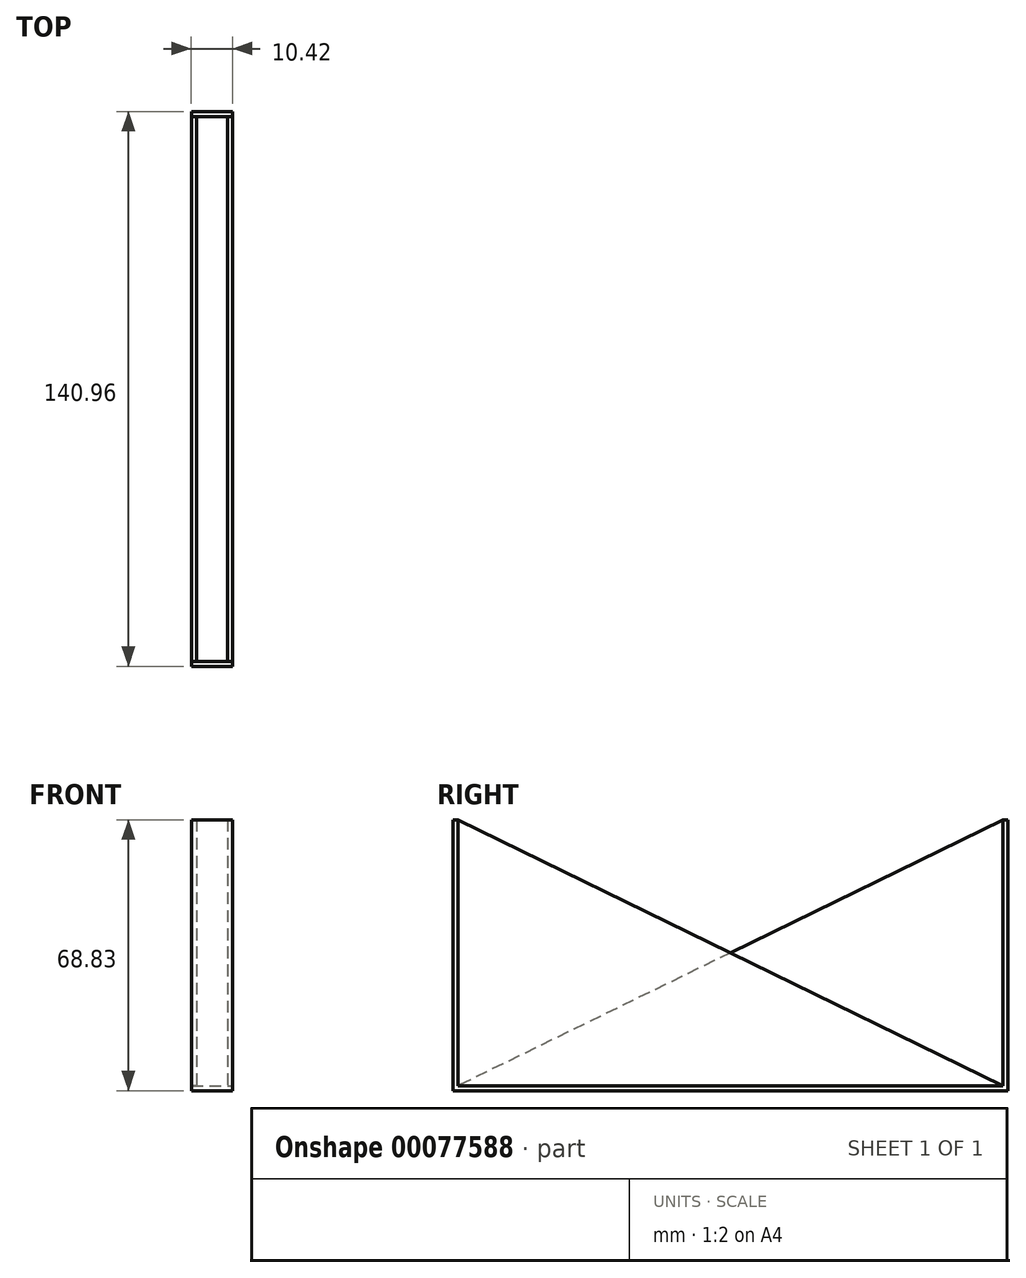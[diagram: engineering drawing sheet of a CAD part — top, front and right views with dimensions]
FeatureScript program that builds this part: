
annotation { "Feature Type Name" : "Feature", "Feature Type Description" : "" }
export const myFeature = defineFeature(function(context is Context, id is Id, definition is map)
    precondition{}
    {
        {
            var Q0;
            Q0=qCreatedBy(makeId("Top.planeOp"),FACE);
            var sketch = newSketch(context, id + "F0", { "sketchPlane" : qUnion([Q0])});
            skLineSegment(sketch, "E0.bottom", {"start": v(5.2, -70.48) * mm, "end": v(-5.2, -70.48) * mm});
            skLineSegment(sketch, "E0.top", {"start": v(5.2, 70.48) * mm, "end": v(-5.2, 70.48) * mm});
            skLineSegment(sketch, "E0.left", {"start": v(5.2, -70.48) * mm, "end": v(5.2, 70.48) * mm});
            skLineSegment(sketch, "E0.right", {"start": v(-5.2, -70.48) * mm, "end": v(-5.2, 70.48) * mm});
            skPoint(sketch, "E0.middle", {"position": v(0, 0) * mm});
            skSolve(sketch);
        }
        {
            var Q0;
            Q0=makeQuery(id+"F0.imprint","IMPRINT",FACE,{"disambiguationData":[TD([[makeQuery(id+"F0.imprint","IMPRINT",EDGE,{"derivedFrom":sQuery(id+"F0.wireOp",EDGE,"E0.bottom")}),-1.0]])]});
            extrude(context, id + "F1", {"entities" : qUnion([Q0]), "depth" : 1.27 * mm});
        }
        {
            var Q0;
            Q0=makeQuery(id+"F1.opExtrude","CAP_FACE",FACE,{"disambiguationData":[OSD([sQuery(id+"F0.wireOp",EDGE,"E0.bottom"),sQuery(id+"F0.wireOp",EDGE,"E0.top"),sQuery(id+"F0.wireOp",EDGE,"E0.left"),sQuery(id+"F0.wireOp",EDGE,"E0.right")])],"isStart":false});
            var sketch = newSketch(context, id + "F2", { "sketchPlane" : qUnion([Q0])});
            skLineSegment(sketch, "E1.bottom", {"start": v(-5.2, -70.48) * mm, "end": v(5.2, -70.48) * mm});
            skLineSegment(sketch, "E1.top", {"start": v(-5.2, -69.22) * mm, "end": v(5.2, -69.22) * mm});
            skLineSegment(sketch, "E1.left", {"start": v(-5.2, -70.48) * mm, "end": v(-5.2, -69.22) * mm});
            skLineSegment(sketch, "E1.right", {"start": v(5.2, -70.48) * mm, "end": v(5.2, -69.22) * mm});
            skLineSegment(sketch, "E2.bottom", {"start": v(-5.2, 70.48) * mm, "end": v(5.2, 70.48) * mm});
            skLineSegment(sketch, "E2.top", {"start": v(-5.2, 69.22) * mm, "end": v(5.2, 69.22) * mm});
            skLineSegment(sketch, "E2.left", {"start": v(-5.2, 70.48) * mm, "end": v(-5.2, 69.22) * mm});
            skLineSegment(sketch, "E2.right", {"start": v(5.2, 70.48) * mm, "end": v(5.2, 69.22) * mm});
            skSolve(sketch);
        }
        {
            var Q0;
            Q0=makeQuery(id+"F2.imprint","IMPRINT",FACE,{"disambiguationData":[TD([[makeQuery(id+"F2.imprint","IMPRINT",EDGE,{"derivedFrom":sQuery(id+"F2.wireOp",EDGE,"E1.bottom")}),-1.0]])]});
            extrude(context, id + "F3", {"entities" : qUnion([Q0]), "operationType" : NewBodyOperationType.ADD, "depth" : 67.56 * mm});
        }
        {
            var Q0;
            Q0=makeQuery(id+"F2.imprint","IMPRINT",FACE,{"disambiguationData":[TD([[makeQuery(id+"F2.imprint","IMPRINT",EDGE,{"derivedFrom":sQuery(id+"F2.wireOp",EDGE,"E2.bottom")}),1.0]])]});
            extrude(context, id + "F4", {"entities" : qUnion([Q0]), "operationType" : NewBodyOperationType.ADD, "depth" : 67.56 * mm});
        }
        {
            var Q0;
            Q0=makeQuery(id+"F4.boolean.opBoolean","MERGE",FACE,{"derivedFrom":[makeQuery(id+"F3.boolean.opBoolean","MERGE",FACE,{"derivedFrom":[makeQuery(id+"F1.opExtrude","SWEPT_FACE",FACE,{"disambiguationData":[OSD([sQuery(id+"F0.wireOp",EDGE,"E0.left")])]}),makeQuery(id+"F3.opExtrude","SWEPT_FACE",FACE,{"disambiguationData":[OSD([sQuery(id+"F2.wireOp",EDGE,"E1.right")])]})]}),makeQuery(id+"F4.opExtrude","SWEPT_FACE",FACE,{"disambiguationData":[OSD([sQuery(id+"F2.wireOp",EDGE,"E2.right")])]})]});
            var sketch = newSketch(context, id + "F5", { "sketchPlane" : qUnion([Q0])});
            skLineSegment(sketch, "E3", {"start": v(-69.22, 68.83) * mm, "end": v(69.22, 1.27) * mm});
            skSolve(sketch);
        }
        {
            var Q0;
            Q0=makeQuery(id+"F5.imprint","IMPRINT",FACE,{"disambiguationData":[TD([[makeQuery(id+"F5.imprint","IMPRINT",EDGE,{"derivedFrom":sQuery(id+"F5.wireOp",EDGE,"E3")}),-1.0]])]});
            extrude(context, id + "F6", {"entities" : qUnion([Q0]), "oppositeDirection" : true, "depth" : 1.27 * mm});
        }
        {
            var Q0;
            Q0=makeQuery(id+"F4.boolean.opBoolean","MERGE",FACE,{"derivedFrom":[makeQuery(id+"F3.boolean.opBoolean","MERGE",FACE,{"derivedFrom":[makeQuery(id+"F1.opExtrude","SWEPT_FACE",FACE,{"disambiguationData":[OSD([sQuery(id+"F0.wireOp",EDGE,"E0.right")])]}),makeQuery(id+"F3.opExtrude","SWEPT_FACE",FACE,{"disambiguationData":[OSD([sQuery(id+"F2.wireOp",EDGE,"E1.left")])]})]}),makeQuery(id+"F4.opExtrude","SWEPT_FACE",FACE,{"disambiguationData":[OSD([sQuery(id+"F2.wireOp",EDGE,"E2.left")])]})]});
            var sketch = newSketch(context, id + "F7", { "sketchPlane" : qUnion([Q0])});
            skLineSegment(sketch, "E4", {"start": v(-69.22, 68.83) * mm, "end": v(69.22, 1.27) * mm});
            skSolve(sketch);
        }
        {
            var Q0;
            Q0=makeQuery(id+"F7.imprint","IMPRINT",FACE,{"disambiguationData":[TD([[makeQuery(id+"F7.imprint","IMPRINT",EDGE,{"derivedFrom":sQuery(id+"F7.wireOp",EDGE,"E4")}),-1.0]])]});
            extrude(context, id + "F8", {"entities" : qUnion([Q0]), "oppositeDirection" : true, "depth" : 1.27 * mm});
        }
    });
